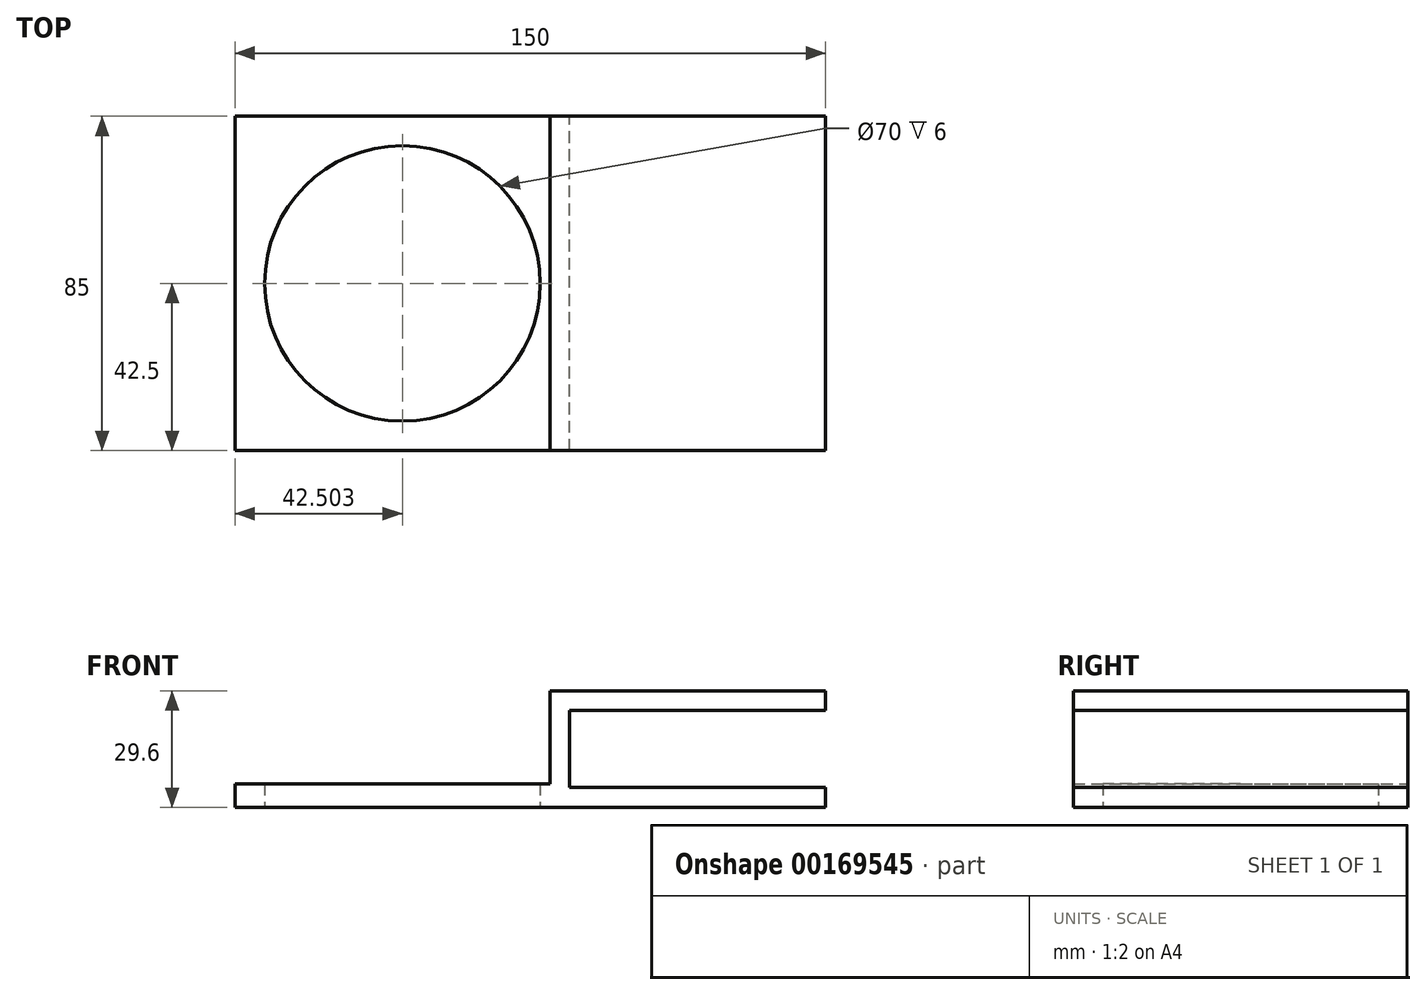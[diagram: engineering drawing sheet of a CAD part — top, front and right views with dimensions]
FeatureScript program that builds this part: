
annotation { "Feature Type Name" : "Feature", "Feature Type Description" : "" }
export const myFeature = defineFeature(function(context is Context, id is Id, definition is map)
    precondition{}
    {
        {
            var Q0;
            Q0=qCreatedBy(makeId("Front.planeOp"),FACE);
            var sketch = newSketch(context, id + "F0", { "sketchPlane" : qUnion([Q0])});
            skLineSegment(sketch, "E0", {"start": v(28.25, 46.7) * mm, "end": v(98.25, 46.7) * mm});
            skLineSegment(sketch, "E1", {"start": v(98.25, 46.7) * mm, "end": v(98.25, 41.7) * mm});
            skLineSegment(sketch, "E2", {"start": v(98.25, 41.7) * mm, "end": v(33.25, 41.7) * mm});
            skLineSegment(sketch, "E3", {"start": v(33.25, 41.7) * mm, "end": v(33.25, 22.1) * mm});
            skLineSegment(sketch, "E4", {"start": v(33.25, 22.1) * mm, "end": v(98.25, 22.1) * mm});
            skLineSegment(sketch, "E5", {"start": v(98.25, 22.1) * mm, "end": v(98.25, 17.1) * mm});
            skLineSegment(sketch, "E6", {"start": v(-51.75, 17.1) * mm, "end": v(-51.75, 23.1) * mm});
            skLineSegment(sketch, "E7", {"start": v(-51.75, 23.1) * mm, "end": v(28.25, 23.1) * mm});
            skLineSegment(sketch, "E8", {"start": v(-51.75, 17.1) * mm, "end": v(98.25, 17.1) * mm});
            skLineSegment(sketch, "E9", {"start": v(28.25, 46.7) * mm, "end": v(28.25, 23.1) * mm});
            skSolve(sketch);
        }
        {
            var Q0;
            Q0=makeQuery(id+"F0.imprint","IMPRINT",FACE,{"disambiguationData":[TD([[makeQuery(id+"F0.imprint","IMPRINT",EDGE,{"derivedFrom":sQuery(id+"F0.wireOp",EDGE,"E0")}),-1.0]])]});
            extrude(context, id + "F1", {"entities" : qUnion([Q0]), "depth" : 85 * mm});
        }
        {
            var Q0;
            Q0=makeQuery(id+"F1.opExtrude","SWEPT_FACE",FACE,{"disambiguationData":[OSD([sQuery(id+"F0.wireOp",EDGE,"E8")])]});
            var sketch = newSketch(context, id + "F2", { "sketchPlane" : qUnion([Q0])});
            skLineSegment(sketch, "E10", {"start": v(-51.75, 85) * mm, "end": v(23.25, 85) * mm});
            skLineSegment(sketch, "E11", {"start": v(-51.75, 85) * mm, "end": v(-51.75, 0) * mm});
            skLineSegment(sketch, "E12", {"start": v(-51.75, 0) * mm, "end": v(23.25, 0) * mm});
            skCircle(sketch, "E13", {"center": v(-9.25, 42.5) * mm, "radius": 35 * mm});
            skLineSegment(sketch, "E14", {"start": v(33.25, 0) * mm, "end": v(33.25, 85) * mm});
            skLineSegment(sketch, "E15", {"start": v(33.25, 85) * mm, "end": v(-51.75, 0) * mm, "construction": true});
            skLineSegment(sketch, "E16", {"start": v(-51.75, 85) * mm, "end": v(33.25, 0) * mm, "construction": true});
            skSolve(sketch);
        }
        {
            var Q0;
            Q0 = qSketchRegion(id + "F2", true);
            extrude(context, id + "F3", {"entities" : qUnion([Q0]), "operationType" : NewBodyOperationType.REMOVE, "oppositeDirection" : true, "depth" : 25 * mm});
        }
    });
